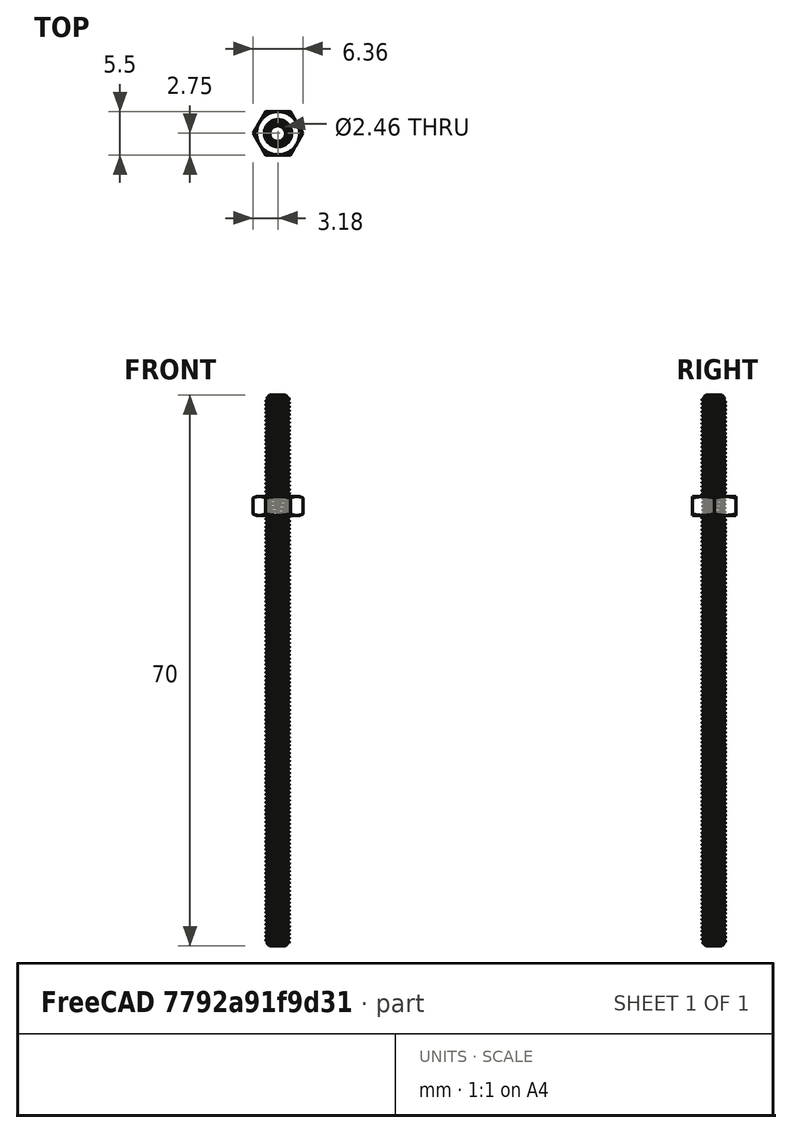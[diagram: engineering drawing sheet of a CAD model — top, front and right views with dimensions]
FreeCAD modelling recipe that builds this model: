
FCSTD DOCUMENT  (FreeCAD 1.1R20260106 (Git shallow))
Label: cartridge-assembly
License: All rights reserved
LicenseURL: https://en.wikipedia.org/wiki/All_rights_reserved
objects: App::Link×3, Part::FeaturePython×2, App::Point×1, Assembly::JointGroup×1, Assembly::AssemblyObject×1
note: 2 computed .brp shape members not serialized (recipe doc carries the construction recipe); baked Part::Feature solids carry a one-line shape summary decoded from their .brp
EXTERNAL_REF file=OTS/luer.FCStd obj=Body
EXTERNAL_REF file=FDM/cartridge-gear.FCStd obj=Body001
EXTERNAL_REF file=FDM/plunger.FCStd obj=Body

FEATURE [App::Point] Origin001
  Role = Origin
FEATURE [Assembly::JointGroup] Joints
FEATURE [App::Link] Body
  LinkedObject = -> <external OTS/luer.FCStd>#Body
FEATURE [App::Link] Body002
  LinkPlacement = pos=(0.0737821,0.0237821,5.17378) rot=(0,0,1;0rad)
  LinkedObject = -> <external FDM/cartridge-gear.FCStd>#Body001
  Placement = pos=(0.0737821,0.0237821,5.17378) rot=(0,0,1;0rad)
FEATURE [Part::FeaturePython] Nut  label="M3-Nut"  # WARN: FeaturePython — macro-defined, semantics opaque (R4)
  Diameter = 4
  Invert = false
  LeftHanded = false
  MatchOuter = false
  OffsetAngle = 0
  Placement = pos=(0.05,0.05,5.7) rot=(0,0,1;0rad)
  Thread = false
  Type = 31
FEATURE [Part::FeaturePython] ThreadedRod  label="M3x70-ThreadedRod"  # WARN: FeaturePython — macro-defined, semantics opaque (R4)
  Diameter = 4
  DiameterCustom = 6
  Invert = false
  LeftHanded = false
  Length = 70
  MatchOuter = false
  OffsetAngle = 0
  PitchCustom = 1
  Placement = pos=(-1.45519e-11,-2.5034e-06,21) rot=(0,0,1;0rad)
  Thread = true
  Type = 4
FEATURE [App::Link] Body003
  LinkPlacement = pos=(-1.19209e-07,0.000680947,-51.8988) rot=(-1,0,0;1.5708rad)
  LinkedObject = -> <external FDM/plunger.FCStd>#Body
  Placement = pos=(-1.19209e-07,0.000680947,-51.8988) rot=(-1,0,0;1.5708rad)
FEATURE [Assembly::AssemblyObject] Assembly
  Group = -> [Joints,Body,Body002,Nut,ThreadedRod,Body003]
  Origin = -> Origin
  Type = Assembly

RESOLVED EXTERNAL PARTS (link-assembly join: the EXTERNAL_REF files above that resolve inside this repo's crawl, each included once):
---- part FDM/cartridge-gear.FCStd = doc fcstd_0ee74163ca0a ----
FCSTD DOCUMENT  (FreeCAD 1.1R20260106 (Git shallow))
Label: cartridge-gear
License: CERN Open Hardware Licence strongly-reciprocal
LicenseURL: https://cern-ohl.web.cern.ch/
objects: Sketcher::SketchObject×2, PartDesign::Pocket×2, Part::FeaturePython×1, PartDesign::FeatureBase×1, PartDesign::Fillet×1, PartDesign::Chamfer×1, PartDesign::Body×1, App::Point×1
note: 20 computed .brp shape members not serialized (recipe doc carries the construction recipe); baked Part::Feature solids carry a one-line shape summary decoded from their .brp

FEATURE [Part::FeaturePython] InvoluteGear  # WARN: FeaturePython — macro-defined, semantics opaque (R4)
  AttacherType = Attacher::AttachEngine3D
  angular_backlash = 0
  backlash = 0
  beta = 0
  clearance = 0.25
  da = 34
  df = 29.5
  double_helix = false
  dw = 32
  head = 0
  head_fillet = 0
  height = 4.5
  module = 1
  numpoints = 7
  pressure_angle = 20
  properties_from_tool = false
  reversed_backlash = false
  root_fillet = 0
  shift = 0
  simple = false
  teeth = 32
  transverse_pitch = 3.14159
  undercut = false
  version = 0.0.4
  expr: angular_backlash = backlash / dw * 360 ° / pi
  expr: dw = teeth * module
FEATURE [PartDesign::FeatureBase] BaseFeature
  BaseFeature = -> InvoluteGear
  Suppressed = false
FEATURE [Sketcher::SketchObject] Sketch
  ArcFitTolerance = 0
  AttachmentSupport = -> [XY_Plane001]
  ExternalTypes = [0]
  FullyConstrained = true
  MakeInternals = false
  MapMode = 5
  sketch-geometry (1):
    g0: Circle CenterX=0 CenterY=0 CenterZ=0 NormalX=0 NormalY=0 NormalZ=1 AngleXU=0 Radius=1.75
  constraints (2):
    c: Coincident(g0,g-1)
    c: Diameter(g0) = 3.5
FEATURE [PartDesign::Pocket] Pocket
  BaseFeature = -> BaseFeature
  Direction = (0,0,-1)
  Length = 5
  Length2 = 5
  Profile = -> Sketch
  ReferenceAxis = -> Sketch [N_Axis]
  Refine = true
  Reversed = true
  SideType = 0
  Suppressed = false
  Type = 0
  Type2 = 0
FEATURE [Sketcher::SketchObject] Sketch001
  ArcFitTolerance = 0
  AttachmentSupport = -> [XY_Plane001]
  ExternalTypes = [0]
  FullyConstrained = true
  MakeInternals = false
  MapMode = 5
  sketch-geometry (7):
    g0: LineSegment StartX=1.61658 StartY=2.8 StartZ=0 EndX=-1.61658 EndY=2.8 EndZ=0
    g1: LineSegment StartX=-1.61658 StartY=2.8 StartZ=0 EndX=-3.23316 EndY=5.0723e-12 EndZ=0
    g2: LineSegment StartX=-3.23316 StartY=5.0723e-12 StartZ=0 EndX=-1.61658 EndY=-2.8 EndZ=0
    g3: LineSegment StartX=-1.61658 StartY=-2.8 StartZ=0 EndX=1.61658 EndY=-2.8 EndZ=0
    g4: LineSegment StartX=1.61658 StartY=-2.8 StartZ=0 EndX=3.23316 EndY=5.8939e-12 EndZ=0
    g5: LineSegment StartX=3.23316 StartY=5.8939e-12 StartZ=0 EndX=1.61658 EndY=2.8 EndZ=0
    g6: Circle [constr] CenterX=0 CenterY=0 CenterZ=0 NormalX=0 NormalY=0 NormalZ=1 AngleXU=0 Radius=3.23316
  constraints (16):
    c: Coincident(g0,g1)
    c: Coincident(g1,g2)
    c: Coincident(g2,g3)
    c: Coincident(g3,g4)
    c: Coincident(g4,g5)
    c: Coincident(g5,g0)
    c: Equal(g0, g1-g5) x5
    c: PointOnObject(g0,g6)
    c: PointOnObject(g1,g6)
    c: PointOnObject(g2,g6)
    c: PointOnObject(g3,g6)
    c: PointOnObject(g4,g6)
    c: PointOnObject(g5,g6)
    c: Coincident(g6,g-1)
    c: Horizontal(g0)
    c: DistanceY(g2,g0) = 5.6
FEATURE [PartDesign::Pocket] Pocket001
  BaseFeature = -> Pocket
  Direction = (0,0,-1)
  Length = 3
  Length2 = 5
  Profile = -> Sketch001
  ReferenceAxis = -> Sketch001 [N_Axis]
  Refine = true
  Reversed = true
  SideType = 0
  Suppressed = false
  Type = 0
  Type2 = 0
FEATURE [PartDesign::Fillet] Fillet
  Base = -> Pocket001 [Edge204,Edge205,Edge200,Edge201,Edge202,Edge203]
  BaseFeature = -> Pocket001
  Radius = 0.4
  Refine = true
  SupportTransform = false
  Suppressed = false
  UseAllEdges = false
FEATURE [PartDesign::Chamfer] Chamfer
  Angle = 45
  Base = -> Fillet [Face206]
  BaseFeature = -> Fillet
  ChamferType = 0
  FlipDirection = false
  Refine = true
  Size = 0.2
  Size2 = 1
  SupportTransform = false
  Suppressed = false
  UseAllEdges = false
FEATURE [PartDesign::Body] Body001  label="Body"
  AllowCompound = false
  BaseFeature = -> InvoluteGear
  Group = -> [BaseFeature,Sketch,Pocket,Sketch001,Pocket001,Fillet,Chamfer]
  Origin = -> Origin001
  Tip = -> Chamfer
FEATURE [App::Point] Origin
  Role = Origin
---- part FDM/plunger.FCStd = doc fcstd_76bcd23fa466 ----
FCSTD DOCUMENT  (FreeCAD 1.1R20260106 (Git shallow))
Label: plunger
License: CERN Open Hardware Licence strongly-reciprocal
LicenseURL: https://cern-ohl.web.cern.ch/
objects: Sketcher::SketchObject×4, PartDesign::Pad×3, PartDesign::Chamfer×3, PartDesign::Pocket×1, PartDesign::Body×1, App::Point×1
note: 30 computed .brp shape members not serialized (recipe doc carries the construction recipe); baked Part::Feature solids carry a one-line shape summary decoded from their .brp

FEATURE [Sketcher::SketchObject] Sketch
  ArcFitTolerance = 0
  AttachmentSupport = -> [XZ_Plane]
  ExternalTypes = [0]
  FullyConstrained = true
  MakeInternals = false
  MapMode = 5
  Placement = pos=(0,0,0) rot=(1,0,0;1.5708rad)
  sketch-geometry (1):
    g0: Circle CenterX=0 CenterY=0 CenterZ=0 NormalX=0 NormalY=0 NormalZ=1 AngleXU=0 Radius=4
  constraints (2):
    c: Coincident(g0,g-1)
    c: Diameter(g0) = 8
FEATURE [PartDesign::Pad] Pad
  Direction = (0,-1,2e-16)
  Length = 10
  Length2 = 10
  Placement = pos=(0,0,0) rot=(1,0,0;1.5708rad)
  Profile = -> Sketch
  ReferenceAxis = -> Sketch [N_Axis]
  Refine = true
  SideType = 0
  Suppressed = false
  Type = 0
  Type2 = 0
FEATURE [Sketcher::SketchObject] Sketch001
  ArcFitTolerance = 0
  AttachmentSupport = -> [XZ_Plane]
  ExternalTypes = [0]
  FullyConstrained = true
  MakeInternals = false
  MapMode = 5
  Placement = pos=(0,0,0) rot=(1,0,0;1.5708rad)
  sketch-geometry (1):
    g0: Circle CenterX=0 CenterY=0 CenterZ=0 NormalX=0 NormalY=0 NormalZ=1 AngleXU=0 Radius=2.25
  constraints (2):
    c: Coincident(g0,g-1)
    c: Diameter(g0) = 4.5
FEATURE [PartDesign::Pad] Pad001
  BaseFeature = -> Pad
  Direction = (0,-1,2e-16)
  Length = 2.25
  Length2 = 10
  Placement = pos=(0,0,0) rot=(1,0,0;1.5708rad)
  Profile = -> Sketch001
  ReferenceAxis = -> Sketch001 [N_Axis]
  Refine = true
  Reversed = true
  SideType = 0
  Suppressed = false
  Type = 0
  Type2 = 0
FEATURE [Sketcher::SketchObject] Sketch002
  ArcFitTolerance = 0
  AttachmentSupport = -> [Pad001]
  ExternalTypes = [0]
  FullyConstrained = true
  MakeInternals = false
  MapMode = 5
  Placement = pos=(0,2.25,0) rot=(-1,0,0;1.5708rad)
  sketch-geometry (1):
    g0: Circle CenterX=0 CenterY=0 CenterZ=0 NormalX=0 NormalY=0 NormalZ=1 AngleXU=0 Radius=3.5
  constraints (2):
    c: Coincident(g0,g-1)
    c: Diameter(g0) = 7
FEATURE [PartDesign::Pad] Pad002
  BaseFeature = -> Pad001
  Direction = (0,1,2e-16)
  Length = 1.5
  Length2 = 10
  Placement = pos=(0,0,0) rot=(1,0,0;1.5708rad)
  Profile = -> Sketch002
  ReferenceAxis = -> Sketch002 [N_Axis]
  Refine = true
  SideType = 0
  Suppressed = false
  Type = 0
  Type2 = 0
FEATURE [PartDesign::Chamfer] Chamfer
  Angle = 45
  Base = -> Pad002 [Edge9,Edge7,Edge2]
  BaseFeature = -> Pad002
  ChamferType = 0
  FlipDirection = false
  Placement = pos=(0,0,0) rot=(1,0,0;1.5708rad)
  Refine = true
  Size = 0.5
  Size2 = 1
  SupportTransform = false
  Suppressed = false
  UseAllEdges = false
FEATURE [Sketcher::SketchObject] Sketch003
  ArcFitTolerance = 0
  AttachmentSupport = -> [Chamfer]
  ExternalTypes = [0]
  FullyConstrained = true
  MakeInternals = false
  MapMode = 5
  Placement = pos=(0,-10,0) rot=(1,0,0;1.5708rad)
  sketch-geometry (1):
    g0: Circle CenterX=0 CenterY=0 CenterZ=0 NormalX=0 NormalY=0 NormalZ=1 AngleXU=0 Radius=1.6
  constraints (2):
    c: Coincident(g0,g-1)
    c: Diameter(g0) = 3.2
FEATURE [PartDesign::Pocket] Pocket
  BaseFeature = -> Chamfer
  Direction = (0,1,-2e-16)
  Length = 8
  Length2 = 5
  Placement = pos=(0,0,0) rot=(1,0,0;1.5708rad)
  Profile = -> Sketch003
  ReferenceAxis = -> Sketch003 [N_Axis]
  Refine = true
  SideType = 0
  Suppressed = false
  Type = 0
  Type2 = 0
FEATURE [PartDesign::Chamfer] Chamfer001
  Angle = 45
  Base = -> Pocket [Edge3,Edge6]
  BaseFeature = -> Pocket
  ChamferType = 0
  FlipDirection = false
  Placement = pos=(0,0,0) rot=(1,0,0;1.5708rad)
  Refine = true
  Size = 0.3
  Size2 = 1
  SupportTransform = false
  Suppressed = false
  UseAllEdges = false
FEATURE [PartDesign::Chamfer] Chamfer002
  Angle = 45
  Base = -> Chamfer001 [Edge15]
  BaseFeature = -> Chamfer001
  ChamferType = 0
  FlipDirection = false
  Placement = pos=(0,0,0) rot=(1,0,0;1.5708rad)
  Refine = true
  Size = 0.4
  Size2 = 1
  SupportTransform = false
  Suppressed = false
  UseAllEdges = false
FEATURE [PartDesign::Body] Body
  AllowCompound = false
  Group = -> [Sketch,Pad,Sketch001,Pad001,Sketch002,Pad002,Chamfer,Sketch003,Pocket,Chamfer001,Chamfer002]
  Origin = -> Origin
  Tip = -> Chamfer002
FEATURE [App::Point] Origin001  label="Origin"
  Role = Origin
---- part OTS/luer.FCStd = doc fcstd_c5db51c11f24 ----
FCSTD DOCUMENT  (FreeCAD 1.1R20260106 (Git shallow))
Label: luer
License: CERN Open Hardware Licence strongly-reciprocal
LicenseURL: https://cern-ohl.web.cern.ch/
objects: Sketcher::SketchObject×2, PartDesign::Pad×2, PartDesign::Fillet×1, PartDesign::Body×1, App::Point×1
note: 14 computed .brp shape members not serialized (recipe doc carries the construction recipe); baked Part::Feature solids carry a one-line shape summary decoded from their .brp

FEATURE [Sketcher::SketchObject] Sketch
  ArcFitTolerance = 1e-06
  AttachmentSupport = -> [XY_Plane]
  ExternalTypes = [0]
  FullyConstrained = true
  MakeInternals = false
  MapMode = 5
  sketch-geometry (9):
    g0: ArcOfCircle CenterX=0 CenterY=-28.4765 CenterZ=0 NormalX=0 NormalY=0 NormalZ=1 AngleXU=0 Radius=35 StartAngle=1.25109 EndAngle=1.8905
    g1: ArcOfCircle CenterX=0 CenterY=28.4765 CenterZ=0 NormalX=0 NormalY=0 NormalZ=1 AngleXU=0 Radius=35 StartAngle=4.39268 EndAngle=5.03209
    g2: LineSegment [constr] StartX=-11 StartY=4.75 StartZ=0 EndX=11 EndY=4.75 EndZ=0
    g3: LineSegment [constr] StartX=-11 StartY=-4.75 StartZ=0 EndX=11 EndY=-4.75 EndZ=0
    g4: LineSegment [constr] StartX=-11 StartY=4.75 StartZ=0 EndX=-11 EndY=-4.75 EndZ=0
    g5: LineSegment [constr] StartX=11 StartY=-4.75 StartZ=0 EndX=11 EndY=4.75 EndZ=0
    g6: ArcOfCircle CenterX=3.22805 CenterY=5.4e-15 CenterZ=0 NormalX=0 NormalY=0 NormalZ=1 AngleXU=0 Radius=15 StartAngle=2.81938 EndAngle=3.46381
    g7: ArcOfCircle CenterX=-3.22805 CenterY=-1e-15 CenterZ=0 NormalX=0 NormalY=0 NormalZ=1 AngleXU=0 Radius=15 StartAngle=5.96097 EndAngle=6.6054
    g8: Circle CenterX=0 CenterY=0 CenterZ=0 NormalX=0 NormalY=0 NormalZ=1 AngleXU=0 Radius=4.75
  constraints (26):
    c: PointOnObject(g0,g-2)
    c: PointOnObject(g1,g-2)
    c: Coincident(g2,g0)
    c: Coincident(g2,g0)
    c: Horizontal(g2)
    c: Coincident(g3,g1)
    c: Coincident(g3,g1)
    c: Horizontal(g3)
    c: DistanceX(g2,g2) = 22
    c: Equal(g2,g3)
    c: DistanceY(g1,g0) = 9.5
    c: Coincident(g4,g0)
    c: Coincident(g4,g1)
    c: Coincident(g5,g1)
    c: Coincident(g5,g0)
    c: DistanceY(g-1,g0) = 4.75
    c: Coincident(g6,g0)
    c: Coincident(g6,g1)
    c: Coincident(g7,g0)
    c: Coincident(g7,g1)
    c: Radius(g0) = 35
    c: Radius(g1) = 35
    c: Radius(g6) = 15
    c: Radius(g7) = 15
    c: Coincident(g8,g-1)
    c: Diameter(g8) = 9.5
FEATURE [PartDesign::Pad] Pad
  Direction = (0,0,1)
  Length = 1.9
  Length2 = 10
  Profile = -> Sketch
  ReferenceAxis = -> Sketch [N_Axis]
  Refine = true
  SideType = 0
  Suppressed = false
  Type = 0
  Type2 = 0
FEATURE [Sketcher::SketchObject] Sketch001
  ArcFitTolerance = 1e-06
  AttachmentSupport = -> [XY_Plane]
  ExternalTypes = [0]
  FullyConstrained = true
  MakeInternals = false
  MapMode = 5
  sketch-geometry (2):
    g0: Circle CenterX=0 CenterY=0 CenterZ=0 NormalX=0 NormalY=0 NormalZ=1 AngleXU=0 Radius=5.85
    g1: Circle CenterX=0 CenterY=0 CenterZ=0 NormalX=0 NormalY=0 NormalZ=1 AngleXU=0 Radius=4.75
  constraints (4):
    c: Coincident(g0,g-1)
    c: Coincident(g1,g0)
    c: Diameter(g1) = 9.5
    c: Diameter(g0) = 11.7
FEATURE [PartDesign::Pad] Pad001
  BaseFeature = -> Pad
  Direction = (0,0,1)
  Length = 56
  Length2 = 10
  Profile = -> Sketch001
  ReferenceAxis = -> Sketch001 [N_Axis]
  Refine = true
  Reversed = true
  SideType = 0
  Suppressed = false
  Type = 0
  Type2 = 0
FEATURE [PartDesign::Fillet] Fillet
  Base = -> Pad001 [Edge5,Edge8,Edge2,Edge1]
  BaseFeature = -> Pad001
  Radius = 4
  Refine = true
  SupportTransform = false
  Suppressed = false
  UseAllEdges = false
FEATURE [PartDesign::Body] Body
  AllowCompound = false
  Group = -> [Sketch,Pad,Sketch001,Pad001,Fillet]
  Origin = -> Origin
  Tip = -> Fillet
FEATURE [App::Point] Origin001  label="Origin"
  Role = Origin
